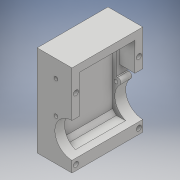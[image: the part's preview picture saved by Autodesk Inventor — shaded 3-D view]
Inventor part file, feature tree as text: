
AUTODESK INVENTOR PART (.ipt)
format: ipt  version: 2018 (Build 220112000, 112)  size: 441,856 bytes
history: native  units: mm
features: sketch x22, projected_geometry x20, extrude x18, hole x4, fillet x3, chamfer x1, mirror x1
ambient origin geometry x8: Origin, YZ Plane, XZ Plane, XY Plane, X Axis, Y Axis, Z Axis, Center Point
bodies: Solid1 (feature_tree)
feature tree (69):
  extrude  "Extrusion1"  Depth=45.0mm
  extrude  "Extrusion2"  Depth=1.95mm
  hole  "Hole1"  [1 undecoded]
  hole  "Hole2"  [1 undecoded]
  fillet  "Fillet1"  Radius=14.0mm
  extrude  "Extrusion3"  Depth=18.5mm
  extrude  "Extrusion4"  Depth=10.0mm
  extrude  "Extrusion5"  Depth=2.0mm
  extrude  "Extrusion6"  Depth=2.0mm
  hole  "Hole3"  [1 undecoded]
  extrude  "Extrusion7"  Depth=0.5mm
  extrude  "Extrusion8"  Depth=5.0mm TaperAngle=0.0deg
  extrude  "Extrusion9"  Depth=10.0mm
  extrude  "Extrusion10"  Depth=10.0mm
  extrude  "Extrusion11"  Depth=14.5mm
  extrude  "Extrusion12"  Depth=14.5mm
  extrude  "Extrusion13"  Depth=5.0mm
  extrude  "Extrusion14"  Depth=5.0mm
  extrude  "Extrusion15"  Depth=5.0mm
  fillet  "Fillet6"  Radius=5.0mm
  extrude  "Extrusion16"  Depth=14.75mm
  extrude  "Extrusion17"  Depth=2.0mm TaperAngle=0.0deg
  chamfer  "Chamfer1"  Distance=20.7mm
  fillet  "Fillet7"  Radius=32.0mm
  hole  "Hole4"  [1 undecoded]
  mirror  "Mirror1"
  extrude  "Extrusion18"  Depth=2.0mm TaperAngle=0.0deg
  sketch  "Sketch1"  dims[d0=24.5mm d1=45.0mm]
  sketch  "Sketch2"  dims[d2=1.95mm d3=0.0mm d4=2.25mm]
  projected_geometry  "Projected Loop1"
  sketch  "Sketch3"  dims[d5=20.0mm d6=2.25mm]
  projected_geometry  "Projected Loop2"
  sketch  "Sketch4"  dims[d7=5.25mm d8=5.25mm d9=14.0mm]
  projected_geometry  "Projected Loop3"
  sketch  "Sketch5"  dims[d10=5.25mm d11=18.5mm]
  projected_geometry  "Projected Loop4"
  sketch  "Sketch6"  dims[d12=10.0mm d13=0.0mm d14=20.5mm]
  projected_geometry  "Projected Loop5"
  sketch  "Sketch7"  dims[d15=2.0mm d16=2.195mm]
  projected_geometry  "Projected Loop6"
  sketch  "Sketch8"  dims[d17=2.0mm]
  projected_geometry  "Projected Loop7"
  sketch  "Sketch9"  dims[d18=2.4mm d19=6.0mm d20=4.4mm d21=2.0mm d22=90.0deg d23=8.0mm d24=20.594885mm d25=20.5mm]
  projected_geometry  "Projected Loop8"
  projected_geometry  "Projected Loop9"
  sketch  "Sketch10"  dims[d26=26.65mm d27=2.0mm]
  projected_geometry  "Projected Loop10"
  projected_geometry  "Projected Loop11"
  sketch  "Sketch11"  dims[d28=2.0mm]
  projected_geometry  "Projected Loop12"
  sketch  "Sketch12"  dims[d29=2.4mm d30=6.0mm d31=4.4mm d32=2.0mm d33=90.0deg d34=8.0mm d35=20.594885mm d36=0.5mm]
  sketch  "Sketch13"  dims[d37=18.0mm d38=5.0mm d39=0.0mm]
  sketch  "Sketch14"  dims[d41=10.0mm d42=0.0mm d43=24.5mm]
  projected_geometry  "Projected Loop13"
  sketch  "Sketch15"  dims[d44=1.15mm d45=0.0mm d46=10.0mm]
  sketch  "Sketch16"  dims[d47=22.0mm d48=14.5mm]
  projected_geometry  "Projected Loop14"
  sketch  "Sketch17"  dims[d49=20.0mm d50=14.5mm]
  projected_geometry  "Projected Loop15"
  sketch  "Sketch18"  dims[d51=24.5mm d52=5.0mm]
  projected_geometry  "Projected Loop16"
  sketch  "Sketch19"  dims[d53=5.0mm d54=2.25mm]
  projected_geometry  "Projected Loop17"
  sketch  "Sketch20"  dims[d55=2.25mm d56=5.0mm d57=5.0mm]
  projected_geometry  "Projected Loop18"
  sketch  "Sketch21"  dims[d58=9.0mm d59=14.75mm]
  projected_geometry  "Projected Loop19"
  projected_geometry  "Projected Loop20"
  sketch  "Sketch22"  dims[d60=4.0mm d61=1.0mm d62=0.0mm d63=20.7mm d64=2.4mm d65=6.0mm d66=4.4mm d67=2.0mm d68=90.0deg d69=8.0mm d70=20.594885mm d72=32.0mm d73=5.0mm d74=0.0mm d75=1.0mm d76=0.0mm d77=12.25mm d78=0.0mm d80=8.0mm d81=4.5mm d82=0.0mm d84=0.2mm d85=0.0mm d86=22.0mm d87=0.5mm d88=0.0mm d91=8.0mm d92=0.0mm d93=5.0mm d94=0.0mm d95=5.0mm d96=0.0mm d97=2.0mm d98=0.2mm d99=0.0mm d100=0.2mm d101=0.0mm d102=2.5mm d103=2.0mm d104=45.0deg d105=1.5mm d106=8.0mm d107=3.2mm d108=5.029mm d109=6.3mm d110=2.0mm d111=90.0deg d112=7.675mm d113=20.594885mm d114=0.1mm d115=0.0mm]
note: 4 required parameter values undecoded (feature->parameter linkage not recoverable at this tier; creation-order binding heuristic only, values carry confidence <= 0.55)
